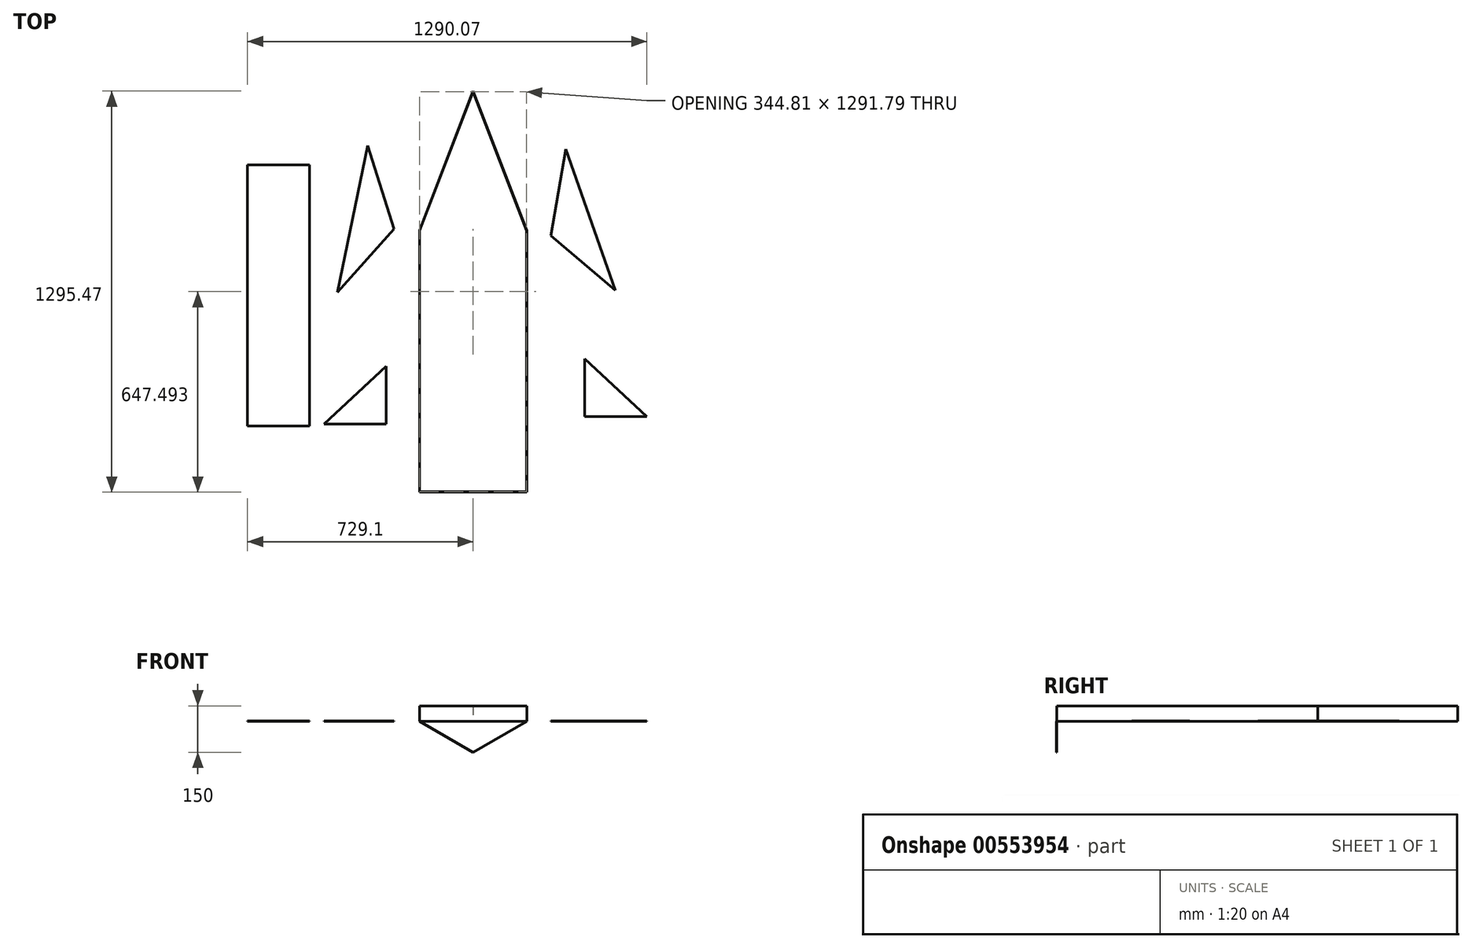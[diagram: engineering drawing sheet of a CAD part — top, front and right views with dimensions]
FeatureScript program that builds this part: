
annotation { "Feature Type Name" : "Feature", "Feature Type Description" : "" }
export const myFeature = defineFeature(function(context is Context, id is Id, definition is map)
    precondition{}
    {
        {
            var Q0;
            Q0=qCreatedBy(makeId("Top.planeOp"),FACE);
            var sketch = newSketch(context, id + "F0", { "sketchPlane" : qUnion([Q0])});
            skLineSegment(sketch, "E0.bottom", {"start": v(0, 0) * mm, "end": v(-173.2, 0) * mm});
            skLineSegment(sketch, "E0.top", {"start": v(0, 0.8) * mm, "end": v(-173.2, 0.8) * mm});
            skLineSegment(sketch, "E0.left", {"start": v(0, 0) * mm, "end": v(0, 0.8) * mm});
            skLineSegment(sketch, "E0.right", {"start": v(-173.2, 0) * mm, "end": v(-173.2, 0.8) * mm});
            skLineSegment(sketch, "E1.bottom", {"start": v(0, 0) * mm, "end": v(173.2, 0) * mm});
            skLineSegment(sketch, "E1.top", {"start": v(0, 0.8) * mm, "end": v(173.2, 0.8) * mm});
            skLineSegment(sketch, "E1.right", {"start": v(173.2, 0) * mm, "end": v(173.2, 0.8) * mm});
            skLineSegment(sketch, "E2.bottom", {"start": v(-173.2, 0) * mm, "end": v(-172.4, 0) * mm});
            skLineSegment(sketch, "E2.top", {"start": v(-173.2, 843.83) * mm, "end": v(-172.4, 843.83) * mm});
            skLineSegment(sketch, "E2.left", {"start": v(-173.2, 0) * mm, "end": v(-173.2, 843.83) * mm});
            skLineSegment(sketch, "E2.right", {"start": v(-172.4, 0) * mm, "end": v(-172.4, 843.83) * mm});
            skLineSegment(sketch, "E3.bottom", {"start": v(173.2, 0) * mm, "end": v(172.4, 0) * mm});
            skLineSegment(sketch, "E3.top", {"start": v(173.2, 843.83) * mm, "end": v(172.4, 843.83) * mm});
            skLineSegment(sketch, "E3.left", {"start": v(173.2, 0) * mm, "end": v(173.2, 843.83) * mm});
            skLineSegment(sketch, "E3.right", {"start": v(172.4, 0) * mm, "end": v(172.4, 843.83) * mm});
            skLineSegment(sketch, "E4", {"start": v(-173.2, 843.83) * mm, "end": v(0, 1294.67) * mm});
            skLineSegment(sketch, "E5", {"start": v(0, 1294.67) * mm, "end": v(173.2, 843.83) * mm});
            skLineSegment(sketch, "E6", {"start": v(-172.4, 843.83) * mm, "end": v(0, 1292.59) * mm});
            skLineSegment(sketch, "E7", {"start": v(0, 1292.59) * mm, "end": v(172.4, 843.83) * mm});
            skSolve(sketch);
        }
        {
            var Q0;
            {var subQ5=sQuery(id+"F0.wireOp",EDGE,"E2.top");Q0=makeQuery(id+"F0.imprint","IMPRINT",FACE,{"disambiguationData":[TD([[makeQuery(id+"F0.imprint","IMPRINT",EDGE,{"derivedFrom":subQ5}),-1.0]])]});}
            extrude(context, id + "F1", {"entities" : qUnion([Q0]), "depth" : 50 * mm});
        }
        {
            var Q0;
            Q0=qSketchRegion(id+"F0",true);
            extrude(context, id + "F2", {"entities" : qUnion([Q0]), "operationType" : NewBodyOperationType.ADD, "depth" : 50 * mm});
        }
        {
            var Q0;
            Q0=qCreatedBy(makeId("Front.planeOp"),FACE);
            var sketch = newSketch(context, id + "F3", { "sketchPlane" : qUnion([Q0])});
            skLineSegment(sketch, "E8", {"start": v(0, 0) * mm, "end": v(0, -100) * mm});
            skLineSegment(sketch, "E9", {"start": v(0, 0) * mm, "end": v(-173.2, 0) * mm});
            skLineSegment(sketch, "E10", {"start": v(0, -100) * mm, "end": v(-173.2, 0) * mm});
            skLineSegment(sketch, "E11.MirrorCS", {"start": v(0, -100) * mm, "end": v(173.2, 0) * mm});
            skLineSegment(sketch, "E12.MirrorCS", {"start": v(0, 0) * mm, "end": v(173.2, 0) * mm});
            skSolve(sketch);
        }
        {
            var Q0;
            Q0=qSketchRegion(id+"F3",true);
            extrude(context, id + "F4", {"entities" : qUnion([Q0]), "depth" : 0.8 * mm});
        }
        {
            var Q0;
            Q0=qCreatedBy(makeId("Top.planeOp"),FACE);
            var sketch = newSketch(context, id + "F5", { "sketchPlane" : qUnion([Q0])});
            skLineSegment(sketch, "E13.bottom", {"start": v(-729.1, 1056.62) * mm, "end": v(-529.1, 1056.62) * mm});
            skLineSegment(sketch, "E13.top", {"start": v(-729.1, 212.79) * mm, "end": v(-529.1, 212.79) * mm});
            skLineSegment(sketch, "E13.left", {"start": v(-729.1, 1056.62) * mm, "end": v(-729.1, 212.79) * mm});
            skLineSegment(sketch, "E13.right", {"start": v(-529.1, 1056.62) * mm, "end": v(-529.1, 212.79) * mm});
            skSolve(sketch);
        }
        {
            var Q0;
            Q0=qSketchRegion(id+"F5",true);
            extrude(context, id + "F6", {"entities" : qUnion([Q0]), "depth" : 0.8 * mm});
        }
        {
            var Q0;
            Q0=qCreatedBy(makeId("Top.planeOp"),FACE);
            var sketch = newSketch(context, id + "F7", { "sketchPlane" : qUnion([Q0])});
            skLineSegment(sketch, "E14", {"start": v(360.97, 243) * mm, "end": v(360.97, 429.6) * mm});
            skLineSegment(sketch, "E15", {"start": v(360.97, 243) * mm, "end": v(560.97, 243) * mm});
            skLineSegment(sketch, "E16", {"start": v(560.97, 243) * mm, "end": v(360.97, 429.6) * mm});
            skSolve(sketch);
        }
        {
            var Q0;
            Q0=qSketchRegion(id+"F7",true);
            extrude(context, id + "F8", {"entities" : qUnion([Q0]), "depth" : 0.8 * mm});
        }
        {
            var Q0;
            Q0=qCreatedBy(makeId("Top.planeOp"),FACE);
            var sketch = newSketch(context, id + "F9", { "sketchPlane" : qUnion([Q0])});
            skLineSegment(sketch, "E17", {"start": v(-281.3, 219.68) * mm, "end": v(-281.3, 406.29) * mm});
            skLineSegment(sketch, "E18", {"start": v(-281.3, 219.68) * mm, "end": v(-481.3, 219.68) * mm});
            skLineSegment(sketch, "E19", {"start": v(-481.3, 219.68) * mm, "end": v(-281.3, 406.29) * mm});
            skSolve(sketch);
        }
        {
            var Q0;
            Q0=qSketchRegion(id+"F9",true);
            extrude(context, id + "F10", {"entities" : qUnion([Q0]), "depth" : 0.8 * mm});
        }
        {
            var Q0;
            Q0=qCreatedBy(makeId("Top.planeOp"),FACE);
            var sketch = newSketch(context, id + "F11", { "sketchPlane" : qUnion([Q0])});
            skLineSegment(sketch, "E20", {"start": v(-340.53, 1118.35) * mm, "end": v(-437.86, 645.3) * mm});
            skLineSegment(sketch, "E21", {"start": v(-437.86, 645.3) * mm, "end": v(-254.89, 848.62) * mm});
            skLineSegment(sketch, "E22", {"start": v(-340.53, 1118.35) * mm, "end": v(-254.89, 848.62) * mm});
            skSolve(sketch);
        }
        {
            var Q0;
            Q0=qSketchRegion(id+"F11",true);
            extrude(context, id + "F12", {"entities" : qUnion([Q0]), "depth" : 0.8 * mm});
        }
        {
            var Q0;
            Q0=qCreatedBy(makeId("Top.planeOp"),FACE);
            var sketch = newSketch(context, id + "F13", { "sketchPlane" : qUnion([Q0])});
            skLineSegment(sketch, "E23", {"start": v(299.82, 1106.73) * mm, "end": v(299.82, 816.41) * mm, "construction": true});
            skLineSegment(sketch, "E24", {"start": v(299.82, 1106.73) * mm, "end": v(250.67, 828.03) * mm});
            skLineSegment(sketch, "E25", {"start": v(299.82, 1106.73) * mm, "end": v(458.98, 650.75) * mm});
            skLineSegment(sketch, "E26", {"start": v(458.98, 650.75) * mm, "end": v(250.67, 828.03) * mm});
            skSolve(sketch);
        }
        {
            var Q0;
            Q0=qSketchRegion(id+"F13",true);
            extrude(context, id + "F14", {"entities" : qUnion([Q0]), "depth" : 0.8 * mm});
        }
    });
